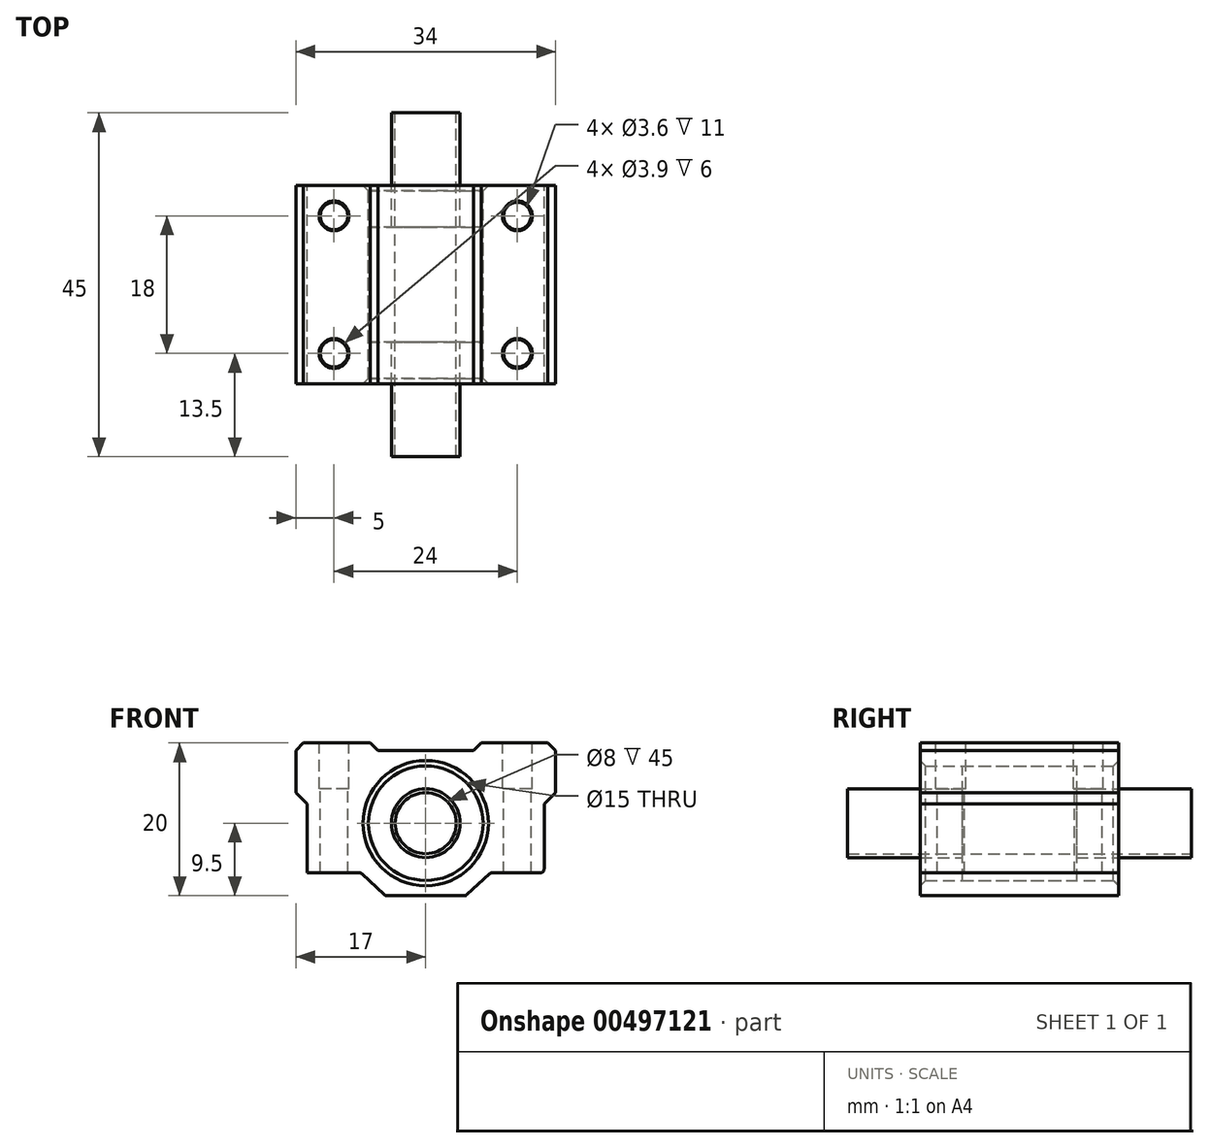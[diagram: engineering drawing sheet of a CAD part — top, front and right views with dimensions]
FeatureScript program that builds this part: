
annotation { "Feature Type Name" : "Feature", "Feature Type Description" : "" }
export const myFeature = defineFeature(function(context is Context, id is Id, definition is map)
    precondition{}
    {
        {
            var Q0;
            Q0=qCreatedBy(makeId("Front.planeOp"),FACE);
            var sketch = newSketch(context, id + "F0", { "sketchPlane" : qUnion([Q0])});
            skCircle(sketch, "E0", {"center": v(0, 0) * mm, "radius": 4 * mm});
            skCircle(sketch, "E1", {"center": v(0, 0) * mm, "radius": 7.5 * mm});
            skLineSegment(sketch, "E2", {"start": v(0, 0) * mm, "end": v(0, 22.9) * mm, "construction": true});
            skLineSegment(sketch, "E3", {"start": v(0, 7.5) * mm, "end": v(0, 9.5) * mm});
            skLineSegment(sketch, "E4", {"start": v(0, 9.5) * mm, "end": v(7.25, 9.5) * mm});
            skLineSegment(sketch, "E5", {"start": v(7.25, 9.5) * mm, "end": v(7.25, 10.5) * mm});
            skLineSegment(sketch, "E6", {"start": v(7.25, 10.5) * mm, "end": v(17, 10.5) * mm});
            skLineSegment(sketch, "E7", {"start": v(17, 10.5) * mm, "end": v(17, 2.5) * mm});
            skLineSegment(sketch, "E8", {"start": v(17, 2.5) * mm, "end": v(15.5, 2.5) * mm});
            skLineSegment(sketch, "E9", {"start": v(15.5, 2.5) * mm, "end": v(15.5, -6.5) * mm});
            skLineSegment(sketch, "E10", {"start": v(15.5, -6.5) * mm, "end": v(8.5, -6.5) * mm});
            skLineSegment(sketch, "E11", {"start": v(8.5, -6.5) * mm, "end": v(5.25, -9.5) * mm});
            skLineSegment(sketch, "E12", {"start": v(5.25, -9.5) * mm, "end": v(0, -9.5) * mm});
            skLineSegment(sketch, "E13", {"start": v(0, -9.5) * mm, "end": v(0, -7.5) * mm});
            skCircle(sketch, "E14", {"center": v(0, 0) * mm, "radius": 4.5 * mm});
            skLineSegment(sketch, "E15.MirrorCS", {"start": v(-5.25, -9.5) * mm, "end": v(0, -9.5) * mm});
            skLineSegment(sketch, "E16.MirrorCS", {"start": v(-8.5, -6.5) * mm, "end": v(-5.25, -9.5) * mm});
            skLineSegment(sketch, "E17.MirrorCS", {"start": v(-17, 2.5) * mm, "end": v(-15.5, 2.5) * mm});
            skLineSegment(sketch, "E18.MirrorCS", {"start": v(-17, 10.5) * mm, "end": v(-17, 2.5) * mm});
            skLineSegment(sketch, "E19.MirrorCS", {"start": v(-7.25, 10.5) * mm, "end": v(-17, 10.5) * mm});
            skLineSegment(sketch, "E20.MirrorCS", {"start": v(-7.25, 9.5) * mm, "end": v(-7.25, 10.5) * mm});
            skLineSegment(sketch, "E21.MirrorCS", {"start": v(0, 9.5) * mm, "end": v(-7.25, 9.5) * mm});
            skLineSegment(sketch, "E22", {"start": v(-15.5, 2.5) * mm, "end": v(-15.5, -6.5) * mm});
            skLineSegment(sketch, "E23", {"start": v(-15.5, -6.5) * mm, "end": v(-8.5, -6.5) * mm});
            skSolve(sketch);
        }
        {
            var Q0;
            {var subQ0=sQuery(id+"F0.wireOp",EDGE,"E3");Q0=makeQuery(id+"F0.imprint","IMPRINT",FACE,{"disambiguationData":[TD([[makeQuery(id+"F0.imprint","IMPRINT",EDGE,{"derivedFrom":subQ0}),-1.0]])]});}
            var Q1;
            {var subQ0=sQuery(id+"F0.wireOp",EDGE,"E3");Q1=makeQuery(id+"F0.imprint","IMPRINT",FACE,{"disambiguationData":[TD([[makeQuery(id+"F0.imprint","IMPRINT",EDGE,{"derivedFrom":subQ0}),1.0]])]});}
            extrude(context, id + "F1", {"entities" : qUnion([Q0, Q1]), "depth" : 26 * mm, "offsetDistance" : 25 * mm, "symmetric" : true});
        }
        {
            var Q0;
            Q0=makeQuery(id+"F1.opExtrude","SWEPT_EDGE",EDGE,{"disambiguationData":[OSD([sQuery(id+"F0.wireOp",EDGE,"E4"),sQuery(id+"F0.wireOp",EDGE,"E5")])]});
            var Q1;
            Q1=makeQuery(id+"F1.opExtrude","SWEPT_EDGE",EDGE,{"disambiguationData":[OSD([sQuery(id+"F0.wireOp",EDGE,"E6"),sQuery(id+"F0.wireOp",EDGE,"E7")])]});
            var Q2;
            Q2=makeQuery(id+"F1.opExtrude","SWEPT_EDGE",EDGE,{"disambiguationData":[OSD([sQuery(id+"F0.wireOp",EDGE,"E20.MirrorCS"),sQuery(id+"F0.wireOp",EDGE,"E21.MirrorCS")])]});
            var Q3;
            Q3=makeQuery(id+"F1.opExtrude","SWEPT_EDGE",EDGE,{"disambiguationData":[OSD([sQuery(id+"F0.wireOp",EDGE,"E18.MirrorCS"),sQuery(id+"F0.wireOp",EDGE,"E19.MirrorCS")])]});
            chamfer(context, id + "F2", {"entities" : qUnion([Q0, Q1, Q2, Q3]), "width" : 1 * mm, "tangentPropagation" : true});
        }
        {
            var Q0;
            Q0=makeQuery(id+"F1.opExtrude","SWEPT_EDGE",EDGE,{"disambiguationData":[OSD([sQuery(id+"F0.wireOp",EDGE,"E7"),sQuery(id+"F0.wireOp",EDGE,"E8")])]});
            var Q1;
            Q1=makeQuery(id+"F1.opExtrude","SWEPT_EDGE",EDGE,{"disambiguationData":[OSD([sQuery(id+"F0.wireOp",EDGE,"E17.MirrorCS"),sQuery(id+"F0.wireOp",EDGE,"E18.MirrorCS")])]});
            chamfer(context, id + "F3", {"entities" : qUnion([Q0, Q1]), "width" : 1.5 * mm, "tangentPropagation" : true});
        }
        {
            var Q0;
            Q0=makeQuery(id+"F1.opExtrude","SWEPT_EDGE",EDGE,{"disambiguationData":[OSD([sQuery(id+"F0.wireOp",EDGE,"E9"),sQuery(id+"F0.wireOp",EDGE,"E10")])]});
            var Q1;
            Q1=makeQuery(id+"F1.opExtrude","SWEPT_EDGE",EDGE,{"disambiguationData":[OSD([sQuery(id+"F0.wireOp",EDGE,"E10"),sQuery(id+"F0.wireOp",EDGE,"E11")])]});
            var Q2;
            Q2=makeQuery(id+"F1.opExtrude","SWEPT_EDGE",EDGE,{"disambiguationData":[OSD([sQuery(id+"F0.wireOp",EDGE,"E11"),sQuery(id+"F0.wireOp",EDGE,"E12")])]});
            var Q3;
            Q3=makeQuery(id+"F1.opExtrude","SWEPT_EDGE",EDGE,{"disambiguationData":[OSD([sQuery(id+"F0.wireOp",EDGE,"E15.MirrorCS"),sQuery(id+"F0.wireOp",EDGE,"E16.MirrorCS")])]});
            var Q4;
            Q4=makeQuery(id+"F1.opExtrude","SWEPT_EDGE",EDGE,{"disambiguationData":[OSD([sQuery(id+"F0.wireOp",EDGE,"E16.MirrorCS"),sQuery(id+"F0.wireOp",EDGE,"O6NMc8kR-GBqP-20ma-tIkf-TSFbQtPsBvN1")])]});
            fillet(context, id + "F4", {"entities" : qUnion([Q0, Q1, Q2, Q3, Q4]), "radius" : .5 * mm, "tangentPropagation" : true, "allowEdgeOverflow" : false});
        }
        {
            var Q0;
            Q0=makeQuery(id+"F1.opExtrude","SWEPT_FACE",FACE,{"disambiguationData":[OSD([sQuery(id+"F0.wireOp",EDGE,"E6")])]});
            var sketch = newSketch(context, id + "F5", { "sketchPlane" : qUnion([Q0])});
            skLineSegment(sketch, "E24.bottom", {"start": v(-12, 9) * mm, "end": v(12, 9) * mm});
            skLineSegment(sketch, "E24.top", {"start": v(-12, -9) * mm, "end": v(12, -9) * mm});
            skLineSegment(sketch, "E24.left", {"start": v(-12, 9) * mm, "end": v(-12, -9) * mm});
            skLineSegment(sketch, "E24.right", {"start": v(12, 9) * mm, "end": v(12, -9) * mm});
            skLineSegment(sketch, "E25", {"start": v(-12, 9) * mm, "end": v(12, -9) * mm});
            skSolve(sketch);
        }
        {
            var Q0;
            Q0=sQuery(id+"F5.wireOp",VERTEX,"E24.right.start");
            var Q1;
            Q1=sQuery(id+"F5.wireOp",VERTEX,"E25.end");
            var Q2;
            Q2=sQuery(id+"F5.wireOp",VERTEX,"E25.start");
            var Q3;
            Q3=sQuery(id+"F5.wireOp",VERTEX,"E24.left.end");
            var Q4;
            Q4=makeQuery(id+"F1.opExtrude","SWEPT_BODY",BODY,{"disambiguationData":[OSD([sQuery(id+"F0.wireOp",EDGE,"E1"),sQuery(id+"F0.wireOp",EDGE,"E3"),sQuery(id+"F0.wireOp",EDGE,"E4"),sQuery(id+"F0.wireOp",EDGE,"E5"),sQuery(id+"F0.wireOp",EDGE,"E6"),sQuery(id+"F0.wireOp",EDGE,"E7"),sQuery(id+"F0.wireOp",EDGE,"E8"),sQuery(id+"F0.wireOp",EDGE,"E9"),sQuery(id+"F0.wireOp",EDGE,"E10"),sQuery(id+"F0.wireOp",EDGE,"E11"),sQuery(id+"F0.wireOp",EDGE,"E12"),sQuery(id+"F0.wireOp",EDGE,"E13")])]});
            hole(context, id + "F6", {"style" : HoleStyle.C_BORE, "endStyle" : HoleEndStyle.THROUGH, "holeDiameter" : 3.6 * mm, "cBoreDiameter" : 3.9 * mm, "cBoreDepth" : 6 * mm, "locations" : qUnion([Q0, Q1, Q2, Q3]), "scope" : qUnion([Q4]), "tappedDepth" : 12 * mm, "tapClearance" : 3});
        }
        {
            var Q0;
            Q0=makeQuery(id+"F6.hole-1.boolean.opBoolean","COPY",EDGE,{"derivedFrom":makeQuery(id+"F6.hole-1.opRevolve","SWEPT_EDGE",EDGE,{"disambiguationData":[OSD([sQuery(id+"F6.hole-1.sketch.wireOp",EDGE,"cbore_start_line_2"),sQuery(id+"F6.hole-1.sketch.wireOp",EDGE,"cbore_start_line_3")])]})});
            var Q1;
            Q1=makeQuery(id+"F6.hole-0.boolean.opBoolean","COPY",EDGE,{"derivedFrom":makeQuery(id+"F6.hole-0.opRevolve","SWEPT_EDGE",EDGE,{"disambiguationData":[OSD([sQuery(id+"F6.hole-0.sketch.wireOp",EDGE,"cbore_start_line_2"),sQuery(id+"F6.hole-0.sketch.wireOp",EDGE,"cbore_start_line_3")])]})});
            var Q2;
            Q2=makeQuery(id+"F1.opExtrude","CAP_EDGE",EDGE,{"disambiguationData":[OSD([sQuery(id+"F0.wireOp",EDGE,"E1")])],"isStart":false});
            var Q3;
            Q3=makeQuery(id+"F1.opExtrude","CAP_EDGE",EDGE,{"disambiguationData":[OSD([sQuery(id+"F0.wireOp",EDGE,"E1")])],"isStart":true});
            var Q4;
            Q4=makeQuery(id+"F6.hole-3.boolean.opBoolean","COPY",EDGE,{"derivedFrom":makeQuery(id+"F6.hole-3.opRevolve","SWEPT_EDGE",EDGE,{"disambiguationData":[OSD([sQuery(id+"F6.hole-3.sketch.wireOp",EDGE,"cbore_start_line_2"),sQuery(id+"F6.hole-3.sketch.wireOp",EDGE,"cbore_start_line_3")])]})});
            var Q5;
            Q5=makeQuery(id+"F6.hole-2.boolean.opBoolean","COPY",EDGE,{"derivedFrom":makeQuery(id+"F6.hole-2.opRevolve","SWEPT_EDGE",EDGE,{"disambiguationData":[OSD([sQuery(id+"F6.hole-2.sketch.wireOp",EDGE,"cbore_start_line_2"),sQuery(id+"F6.hole-2.sketch.wireOp",EDGE,"cbore_start_line_3")])]})});
            chamfer(context, id + "F7", {"entities" : qUnion([Q0, Q1, Q2, Q3, Q4, Q5]), "width" : .7 * mm, "tangentPropagation" : true});
        }
        {
            var Q0;
            Q0=makeQuery(id+"F0.imprint","IMPRINT",FACE,{"disambiguationData":[TD([[makeQuery(id+"F0.imprint","IMPRINT",EDGE,{"derivedFrom":sQuery(id+"F0.wireOp",EDGE,"E14")}),-1.0]])]});
            extrude(context, id + "F8", {"entities" : qUnion([Q0]), "depth" : 15 * mm, "offsetDistance" : 25 * mm, "symmetric" : true});
        }
        {
            var Q0;
            Q0=makeQuery(id+"F0.imprint","IMPRINT",FACE,{"disambiguationData":[TD([[makeQuery(id+"F0.imprint","IMPRINT",EDGE,{"derivedFrom":sQuery(id+"F0.wireOp",EDGE,"E0")}),-1.0]])]});
            extrude(context, id + "F9", {"entities" : qUnion([Q0]), "operationType" : NewBodyOperationType.ADD, "depth" : 45 * mm, "symmetric" : true});
        }
    });
